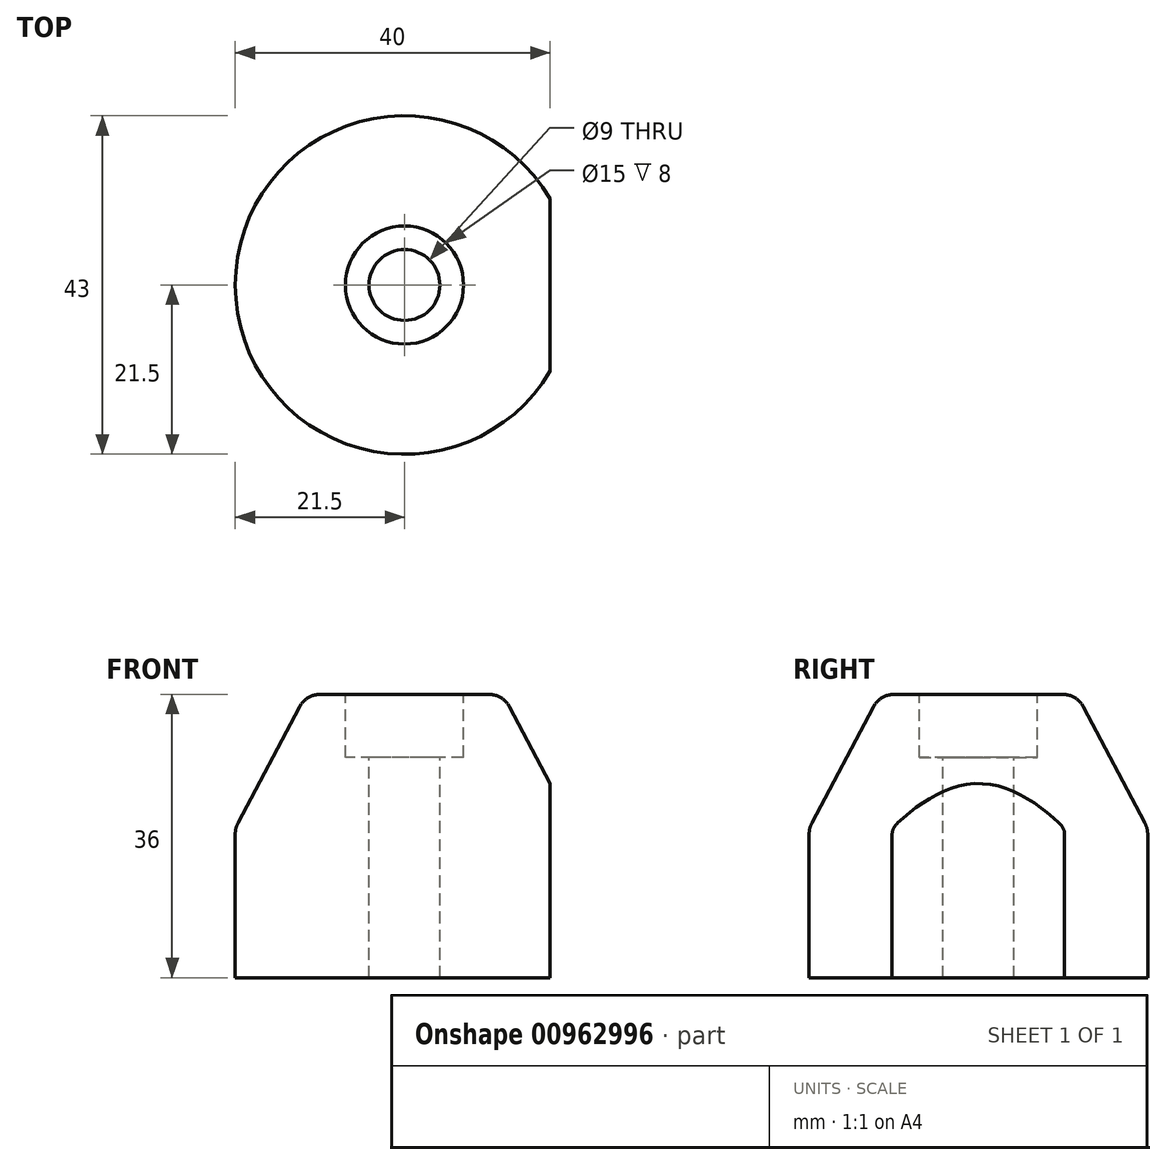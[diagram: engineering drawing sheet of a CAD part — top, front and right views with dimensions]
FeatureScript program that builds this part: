
annotation { "Feature Type Name" : "Feature", "Feature Type Description" : "" }
export const myFeature = defineFeature(function(context is Context, id is Id, definition is map)
    precondition{}
    {
        {
            var Q0;
            Q0=qCreatedBy(makeId("Top.planeOp"),FACE);
            var sketch = newSketch(context, id + "F0", { "sketchPlane" : qUnion([Q0])});
            skCircle(sketch, "E0", {"center": v(0, 0) * mm, "radius": 21.5 * mm});
            skSolve(sketch);
        }
        {
            var Q0;
            Q0=makeQuery(id+"F0.imprint","IMPRINT",FACE,{"disambiguationData":[TD([[makeQuery(id+"F0.imprint","IMPRINT",EDGE,{"derivedFrom":sQuery(id+"F0.wireOp",EDGE,"E0")}),1.0]])]});
            extrude(context, id + "F1", {"entities" : qUnion([Q0]), "depth" : 19 * mm, "offsetDistance" : 25 * mm});
        }
        {
            var Q0;
            Q0=qCreatedBy(makeId("Top.planeOp"),FACE);
            cPlane(context, id + "F2", {"entities" : qUnion([Q0]), "cplaneType" : CPlaneType.OFFSET, "offset" : 36 * mm, "width" : 150 * mm, "height" : 150 * mm});
        }
        {
            var Q0;
            Q0=qCreatedBy(id+"F2.planeOp",FACE);
            var sketch = newSketch(context, id + "F3", { "sketchPlane" : qUnion([Q0])});
            skPoint(sketch, "E1", {"position": v(0, 0) * mm});
            skCircle(sketch, "E2", {"center": v(0, 0) * mm, "radius": 12.5 * mm});
            skSolve(sketch);
        }
        {
            var Q1;
            Q1=makeQuery(id+"F3.imprint","IMPRINT",FACE,{"disambiguationData":[TD([[makeQuery(id+"F3.imprint","IMPRINT",EDGE,{"derivedFrom":sQuery(id+"F3.wireOp",EDGE,"E2")}),1.0]])]});
            var Q2;
            Q2=makeQuery(id+"F1.opExtrude","CAP_FACE",FACE,{"disambiguationData":[OSD([sQuery(id+"F0.wireOp",EDGE,"E0")])],"isStart":false});
            loft(context, id + "F4", {"operationType" : NewBodyOperationType.ADD, "sheetProfilesArray" : [{ "sheetProfileEntities" : qUnion([Q1]) }, { "sheetProfileEntities" : qUnion([Q2]) }]});
        }
        {
            var Q0;
            Q0=sQuery(id+"F3.wireOp",VERTEX,"E1");
            var Q1;
            Q1=makeQuery(id+"F1.opExtrude","SWEPT_BODY",BODY,{"disambiguationData":[OSD([sQuery(id+"F0.wireOp",EDGE,"E0")])]});
            hole(context, id + "F5", {"style" : HoleStyle.C_BORE, "endStyle" : HoleEndStyle.THROUGH, "holeDiameter" : 9 * mm, "cBoreDiameter" : 15 * mm, "cBoreDepth" : 8 * mm, "majorDiameter" : 8 * mm, "isTappedThrough" : true, "tappedDepth" : 12.6 * mm, "tapClearance" : 3, "startFromSketch" : true, "locations" : qUnion([Q0]), "scope" : qUnion([Q1])});
        }
        {
            var Q0;
            Q0=qCreatedBy(makeId("Right.planeOp"),FACE);
            cPlane(context, id + "F6", {"entities" : qUnion([Q0]), "cplaneType" : CPlaneType.OFFSET, "offset" : 21.5 * mm, "width" : 150 * mm, "height" : 150 * mm});
        }
        {
            var Q0;
            Q0=qCreatedBy(id+"F6.planeOp",FACE);
            var sketch = newSketch(context, id + "F7", { "sketchPlane" : qUnion([Q0])});
            skPoint(sketch, "E3", {"position": v(-31.1, 26.04) * mm});
            skPoint(sketch, "E4", {"position": v(32.28, 26.04) * mm});
            skPoint(sketch, "E5", {"position": v(32.28, 0) * mm});
            skPoint(sketch, "E6", {"position": v(-31.1, 0) * mm});
            skLineSegment(sketch, "E7.bottom", {"start": v(-31.1, 26.04) * mm, "end": v(32.28, 26.04) * mm});
            skLineSegment(sketch, "E7.top", {"start": v(-31.1, 0) * mm, "end": v(32.28, 0) * mm});
            skLineSegment(sketch, "E7.left", {"start": v(-31.1, 26.04) * mm, "end": v(-31.1, 0) * mm});
            skLineSegment(sketch, "E7.right", {"start": v(32.28, 26.04) * mm, "end": v(32.28, 0) * mm});
            skSolve(sketch);
        }
        {
            var Q0;
            Q0 = qSketchRegion(id + "F7", true);
            extrude(context, id + "F8", {"entities" : qUnion([Q0]), "operationType" : NewBodyOperationType.REMOVE, "oppositeDirection" : true, "depth" : 3 * mm, "offsetDistance" : 25 * mm});
        }
        {
            var Q0;
            Q0=makeQuery(id+"F4.opLoft","MID_CAP_EDGE",EDGE,{"disambiguationData":[OSD([sQuery(id+"F3.wireOp",EDGE,"E2")])],"capPos":0.0});
            fillet(context, id + "F9", {"entities" : qUnion([Q0]), "radius" : 3 * mm, "tangentPropagation" : true, "allowEdgeOverflow" : false});
        }
        {
            var Q0;
            {var subQ0=sQuery(id+"F0.wireOp",EDGE,"E0");Q0=makeQuery(id+"F4.boolean.opBoolean","MERGE",EDGE,{"derivedFrom":[makeQuery(id+"F1.opExtrude","CAP_EDGE",EDGE,{"disambiguationData":[OSD([subQ0])],"isStart":false}),makeQuery(id+"F4.opLoft","MID_CAP_EDGE",EDGE,{"disambiguationData":[OSD([subQ0])],"capPos":1.0})]});}
            fillet(context, id + "F10", {"entities" : qUnion([Q0]), "radius" : 3 * mm, "tangentPropagation" : true, "allowEdgeOverflow" : false});
        }
    });
